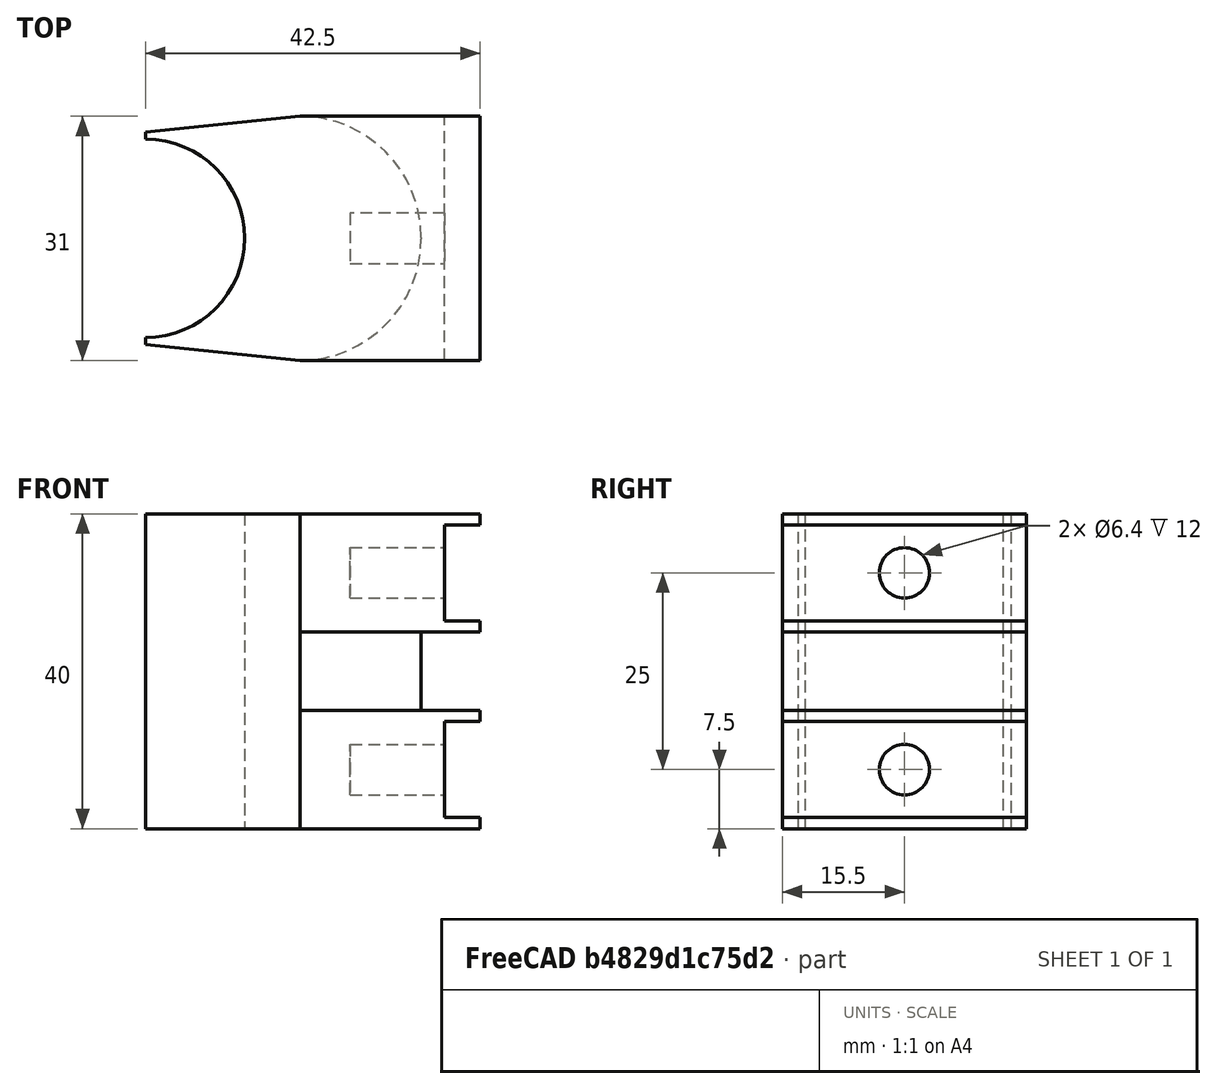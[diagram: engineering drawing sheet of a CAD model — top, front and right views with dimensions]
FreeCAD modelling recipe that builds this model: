
FCSTD DOCUMENT  (FreeCAD 0.21R33771 (Git))
Label: J-Pole_433_Clamp
Comment: J-Pole antenna clamp holder for a 25 mm pole (optional)
License: CC BY-SA 4.0 (SPDX-ID: CC-BY-SA-4.0)
LicenseURL: https://creativecommons.org/licenses/by-sa/4.0/legalcode.txt
objects: Sketcher::SketchObject×8, PartDesign::Pocket×5, PartDesign::Pad×3, PartDesign::Fillet×1, PartDesign::Body×1, Mesh::Feature×1
note: 27 computed .brp shape members not serialized (recipe doc carries the construction recipe); baked Part::Feature solids carry a one-line shape summary decoded from their .brp

FEATURE [Sketcher::SketchObject] Sketch
  FullyConstrained = true
  MapMode = 5
  Support = -> [XY_Plane]
  sketch-geometry (4):
    g0: LineSegment StartX=-12.5 StartY=15.5 StartZ=0 EndX=30 EndY=15.5 EndZ=0
    g1: LineSegment StartX=30 StartY=15.5 StartZ=0 EndX=30 EndY=-15.5 EndZ=0
    g2: LineSegment StartX=30 StartY=-15.5 StartZ=0 EndX=-12.5 EndY=-15.5 EndZ=0
    g3: LineSegment StartX=-12.5 StartY=-15.5 StartZ=0 EndX=-12.5 EndY=15.5 EndZ=0
  constraints (12):
    c: Coincident(g0,g1)
    c: Coincident(g1,g2)
    c: Coincident(g2,g3)
    c: Coincident(g3,g0)
    c: Horizontal(g0)
    c: Horizontal(g2)
    c: Vertical(g1)
    c: Vertical(g3)
    c: DistanceX(g0,g0) = 42.5
    c: DistanceY(g3,g3) = 31
    c: Distance(g-1,g3) = 12.5
    c: Distance(g-1,g0) = 15.5
FEATURE [PartDesign::Pad] Pad
  Direction = (0,0,1)
  Length = 15
  Length2 = 10
  Profile = -> Sketch
  ReferenceAxis = -> Sketch [N_Axis]
  Type = 0
FEATURE [Sketcher::SketchObject] Sketch001
  ExternalGeometry = -> [Pad]
  FullyConstrained = true
  MapMode = 5
  Placement = pos=(30,0,0) rot=(0.57735,0.57735,0.57735;2.0944rad)
  Support = -> [Pad]
  sketch-geometry (4):
    g0: LineSegment StartX=-15.5 StartY=13.6 StartZ=0 EndX=15.5 EndY=13.6 EndZ=0
    g1: LineSegment StartX=15.5 StartY=13.6 StartZ=0 EndX=15.5 EndY=1.4 EndZ=0
    g2: LineSegment StartX=15.5 StartY=1.4 StartZ=0 EndX=-15.5 EndY=1.4 EndZ=0
    g3: LineSegment StartX=-15.5 StartY=1.4 StartZ=0 EndX=-15.5 EndY=13.6 EndZ=0
  constraints (12):
    c: Coincident(g0,g1)
    c: Coincident(g1,g2)
    c: Coincident(g2,g3)
    c: Coincident(g3,g0)
    c: Horizontal(g0)
    c: Horizontal(g2)
    c: Vertical(g1)
    c: Vertical(g3)
    c: PointOnObject(g0,g-3)
    c: PointOnObject(g1,g-4)
    c: DistanceY(g3,g3) = 12.2
    c: Distance(g-1,g2) = 1.4
FEATURE [PartDesign::Pocket] Pocket
  BaseFeature = -> Pad
  Direction = (-1,0,0)
  Length = 4.5
  Length2 = 5
  Profile = -> Sketch001
  ReferenceAxis = -> Sketch001 [N_Axis]
  Type = 0
FEATURE [Sketcher::SketchObject] Sketch002
  ExternalGeometry = -> [Pocket]
  FullyConstrained = true
  MapMode = 5
  Placement = pos=(25.5,0,0) rot=(0.57735,0.57735,0.57735;2.0944rad)
  Support = -> [Pocket]
  sketch-geometry (1):
    g0: Circle CenterX=0 CenterY=7.5 CenterZ=0 NormalX=0 NormalY=0 NormalZ=1 AngleXU=0 Radius=3.2
  constraints (3):
    c: PointOnObject(g0,g-2)
    c: Radius(g0) = 3.2
    c: Distance(g0,g-3) = 7.5
FEATURE [PartDesign::Pocket] Pocket001
  BaseFeature = -> Pocket
  Direction = (-1,0,0)
  Length = 12
  Length2 = 5
  Profile = -> Sketch002
  ReferenceAxis = -> Sketch002 [N_Axis]
  Type = 0
FEATURE [Sketcher::SketchObject] Sketch003
  ExternalGeometry = -> [Pocket001]
  FullyConstrained = true
  MapMode = 5
  Placement = pos=(0,0,15) rot=(0,0,1;0rad)
  Support = -> [Pocket001]
  sketch-geometry (4):
    g0: LineSegment StartX=-12.5 StartY=15.5 StartZ=0 EndX=22.5 EndY=15.5 EndZ=0
    g1: LineSegment StartX=22.5 StartY=15.5 StartZ=0 EndX=22.5 EndY=-15.5 EndZ=0
    g2: LineSegment StartX=22.5 StartY=-15.5 StartZ=0 EndX=-12.5 EndY=-15.5 EndZ=0
    g3: LineSegment StartX=-12.5 StartY=-15.5 StartZ=0 EndX=-12.5 EndY=15.5 EndZ=0
  constraints (11):
    c: Coincident(g0,g1)
    c: Coincident(g1,g2)
    c: Coincident(g2,g3)
    c: Coincident(g3,g0)
    c: Horizontal(g0)
    c: Horizontal(g2)
    c: Vertical(g1)
    c: Vertical(g3)
    c: Coincident(g0,g-3)
    c: PointOnObject(g1,g-4)
    c: DistanceX(g2,g2) = 35
FEATURE [PartDesign::Pad] Pad001
  BaseFeature = -> Pocket001
  Direction = (0,0,1)
  Length = 10
  Length2 = 10
  Profile = -> Sketch003
  ReferenceAxis = -> Sketch003 [N_Axis]
  Type = 0
FEATURE [PartDesign::Fillet] Fillet
  Base = -> Pad001 [Edge36,Edge25]
  BaseFeature = -> Pad001
  Radius = 15.4
  SupportTransform = false
  UseAllEdges = false
FEATURE [Sketcher::SketchObject] Sketch004
  ExternalGeometry = -> [Fillet]
  FullyConstrained = true
  MapMode = 5
  Placement = pos=(0,0,25) rot=(0,0,1;0rad)
  Support = -> [Fillet]
  sketch-geometry (4):
    g0: LineSegment StartX=-12.5 StartY=15.5 StartZ=0 EndX=30 EndY=15.5 EndZ=0
    g1: LineSegment StartX=30 StartY=15.5 StartZ=0 EndX=30 EndY=-15.5 EndZ=0
    g2: LineSegment StartX=30 StartY=-15.5 StartZ=0 EndX=-12.5 EndY=-15.5 EndZ=0
    g3: LineSegment StartX=-12.5 StartY=-15.5 StartZ=0 EndX=-12.5 EndY=15.5 EndZ=0
  constraints (10):
    c: Coincident(g0,g1)
    c: Coincident(g1,g2)
    c: Coincident(g2,g3)
    c: Coincident(g3,g0)
    c: Horizontal(g0)
    c: Horizontal(g2)
    c: Vertical(g1)
    c: Vertical(g3)
    c: Coincident(g0,g-4)
    c: Coincident(g1,g-3)
FEATURE [PartDesign::Pad] Pad002
  BaseFeature = -> Fillet
  Direction = (0,0,1)
  Length = 15
  Length2 = 10
  Profile = -> Sketch004
  ReferenceAxis = -> Sketch004 [N_Axis]
  Type = 0
FEATURE [Sketcher::SketchObject] Sketch005
  ExternalGeometry = -> [Pad002]
  FullyConstrained = true
  MapMode = 5
  Placement = pos=(30,0,0) rot=(0.57735,0.57735,0.57735;2.0944rad)
  Support = -> [Pad002]
  sketch-geometry (4):
    g0: LineSegment StartX=-15.5 StartY=38.6 StartZ=0 EndX=15.5 EndY=38.6 EndZ=0
    g1: LineSegment StartX=15.5 StartY=38.6 StartZ=0 EndX=15.5 EndY=26.4 EndZ=0
    g2: LineSegment StartX=15.5 StartY=26.4 StartZ=0 EndX=-15.5 EndY=26.4 EndZ=0
    g3: LineSegment StartX=-15.5 StartY=26.4 StartZ=0 EndX=-15.5 EndY=38.6 EndZ=0
  constraints (12):
    c: Coincident(g0,g1)
    c: Coincident(g1,g2)
    c: Coincident(g2,g3)
    c: Coincident(g3,g0)
    c: Horizontal(g0)
    c: Horizontal(g2)
    c: Vertical(g1)
    c: Vertical(g3)
    c: PointOnObject(g0,g-3)
    c: PointOnObject(g1,g-4)
    c: DistanceY(g3,g3) = 12.2
    c: Distance(g0,g-5) = 1.4
FEATURE [PartDesign::Pocket] Pocket002
  BaseFeature = -> Pad002
  Direction = (-1,0,0)
  Length = 4.5
  Length2 = 5
  Profile = -> Sketch005
  ReferenceAxis = -> Sketch005 [N_Axis]
  Type = 0
FEATURE [Sketcher::SketchObject] Sketch006
  ExternalGeometry = -> [Pocket002]
  FullyConstrained = true
  MapMode = 5
  Placement = pos=(25.5,0,0) rot=(0.57735,0.57735,0.57735;2.0944rad)
  Support = -> [Pocket002]
  sketch-geometry (1):
    g0: Circle CenterX=0 CenterY=32.5 CenterZ=0 NormalX=0 NormalY=0 NormalZ=1 AngleXU=0 Radius=3.2
  constraints (3):
    c: PointOnObject(g0,g-2)
    c: Radius(g0) = 3.2
    c: Distance(g0,g-3) = 7.5
FEATURE [PartDesign::Pocket] Pocket003
  BaseFeature = -> Pocket002
  Direction = (-1,0,0)
  Length = 12
  Length2 = 5
  Profile = -> Sketch006
  ReferenceAxis = -> Sketch006 [N_Axis]
  Type = 0
FEATURE [Sketcher::SketchObject] Sketch007
  ExternalGeometry = -> [Pocket003]
  FullyConstrained = true
  MapMode = 5
  Placement = pos=(0,0,40) rot=(0,0,1;0rad)
  Support = -> [Pocket003]
  sketch-geometry (7):
    g0: LineSegment StartX=-12.5 StartY=15.5 StartZ=0 EndX=7.1 EndY=15.5 EndZ=0
    g1: LineSegment StartX=7.1 StartY=15.5 StartZ=0 EndX=-12.5 EndY=13.5 EndZ=0
    g2: LineSegment StartX=-12.5 StartY=13.5 StartZ=0 EndX=-12.5 EndY=15.5 EndZ=0
    g3: LineSegment StartX=-12.5 StartY=-13.5 StartZ=0 EndX=-12.5 EndY=-15.5 EndZ=0
    g4: LineSegment StartX=-12.5 StartY=-15.5 StartZ=0 EndX=7.1 EndY=-15.5 EndZ=0
    g5: LineSegment StartX=7.1 StartY=-15.5 StartZ=0 EndX=-12.5 EndY=-13.5 EndZ=0
    g6: Circle CenterX=-12.5 CenterY=0 CenterZ=0 NormalX=0 NormalY=0 NormalZ=1 AngleXU=0 Radius=12.6
  constraints (17):
    c: PointOnObject(g1,g-3)
    c: Coincident(g2,g1)
    c: Coincident(g2,g0)
    c: PointOnObject(g3,g-3)
    c: Coincident(g3,g-5)
    c: Coincident(g4,g3)
    c: Coincident(g5,g4)
    c: Coincident(g5,g3)
    c: Distance(g1,g3) = 27
    c: Coincident(g4,g-7)
    c: Coincident(g0,g-4)
    c: Distance(g3,g3) = 2
    c: Coincident(g0,g-6)
    c: Coincident(g1,g0)
    c: Radius(g6) = 12.6
    c: PointOnObject(g6,g-3)
    c: PointOnObject(g6,g-1)
FEATURE [PartDesign::Pocket] Pocket004
  BaseFeature = -> Pocket003
  Direction = (0,0,-1)
  Length = 5
  Length2 = 5
  Profile = -> Sketch007
  ReferenceAxis = -> Sketch007 [N_Axis]
  Type = 1
FEATURE [PartDesign::Body] Body
  Group = -> [Sketch,Pad,Sketch001,Pocket,Sketch002,Pocket001,Sketch003,Pad001,Fillet,Sketch004,Pad002,Sketch005,Pocket002,Sketch006,Pocket003,Sketch007,Pocket004]
  Origin = -> Origin
  Tip = -> Pocket004
FEATURE [Mesh::Feature] Mesh  label="J-Pole_433_Clamp"
